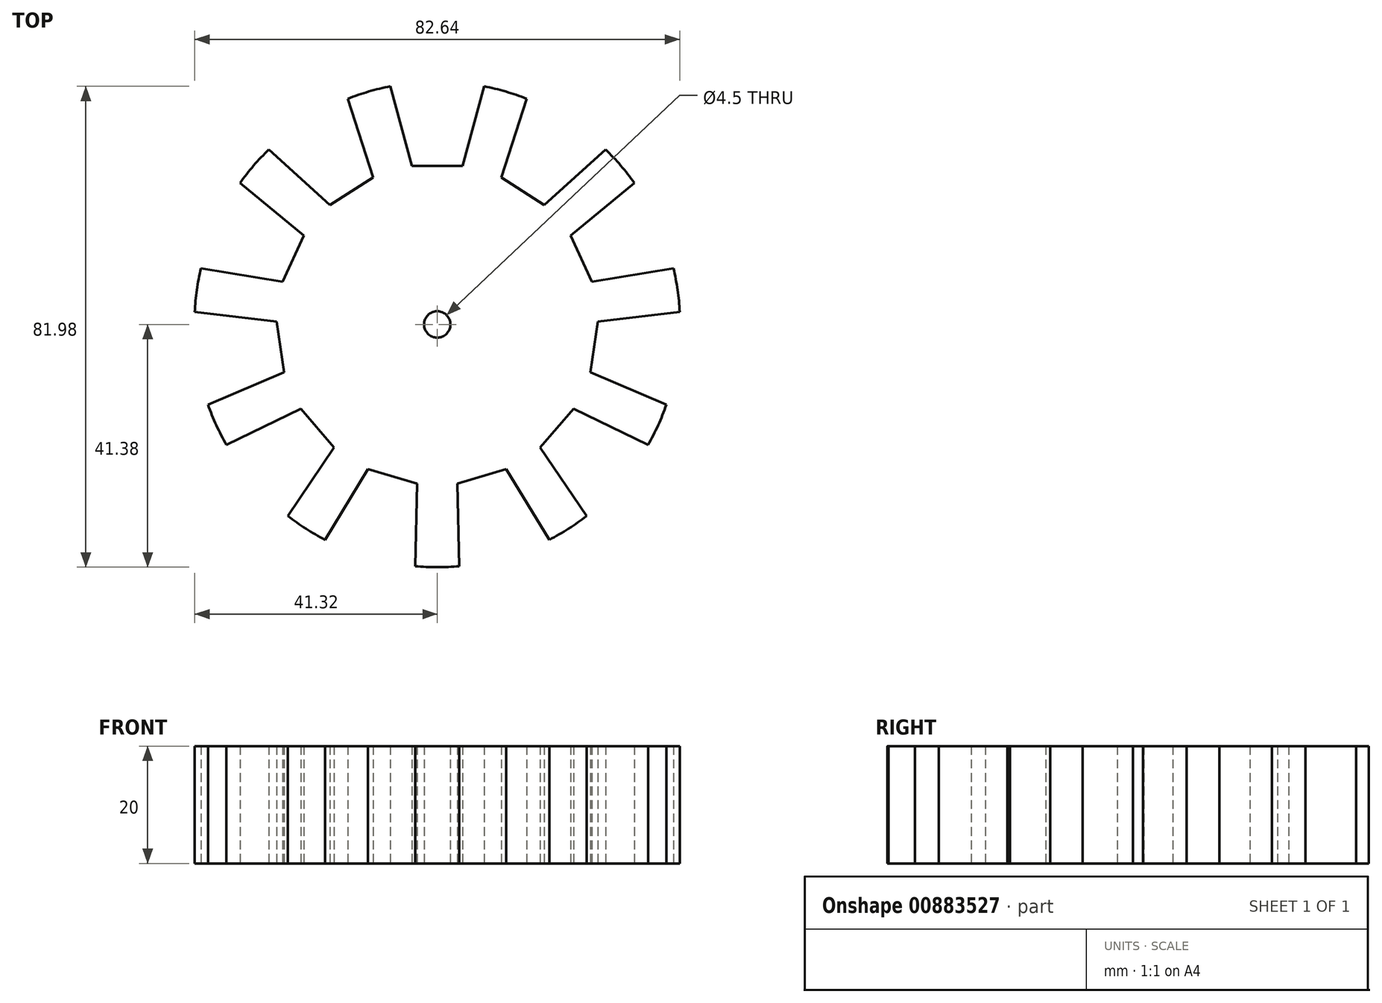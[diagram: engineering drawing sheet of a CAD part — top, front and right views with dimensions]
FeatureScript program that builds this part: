
annotation { "Feature Type Name" : "Feature", "Feature Type Description" : "" }
export const myFeature = defineFeature(function(context is Context, id is Id, definition is map)
    precondition{}
    {
        {
            var Q0;
            Q0=qCreatedBy(makeId("Top.planeOp"),FACE);
            var sketch = newSketch(context, id + "F0", { "sketchPlane" : qUnion([Q0])});
            skCircle(sketch, "E0", {"center": v(0, 0) * mm, "radius": 41.38 * mm});
            skLineSegment(sketch, "E1", {"start": v(-8, 40.6) * mm, "end": v(-4.35, 27) * mm});
            skLineSegment(sketch, "E2", {"start": v(-4.35, 27) * mm, "end": v(0, 27) * mm});
            skLineSegment(sketch, "E3.MirrorCS", {"start": v(8, 40.6) * mm, "end": v(4.35, 27) * mm});
            skLineSegment(sketch, "E4.MirrorCS", {"start": v(4.35, 27) * mm, "end": v(0, 27) * mm});
            skCircle(sketch, "E5", {"center": v(0, 0) * mm, "radius": 2.25 * mm});
            skSolve(sketch);
        }
        {
            var Q0;
            {var subQ1=sQuery(id+"F0.wireOp",EDGE,"E1");Q0=makeQuery(id+"F0.imprint","IMPRINT",FACE,{"disambiguationData":[TD([[makeQuery(id+"F0.imprint","IMPRINT",EDGE,{"derivedFrom":subQ1}),-1.0]])]});}
            extrude(context, id + "F1", {"entities" : qUnion([Q0]), "depth" : 20 * mm, "offsetDistance" : 25 * mm});
        }
        {
            var Q0;
            Q0=makeQuery(id+"F1.opExtrude","SWEPT_FACE",FACE,{"disambiguationData":[OSD([sQuery(id+"F0.wireOp",EDGE,"E1")])]});
            var Q1;
            Q1=makeQuery(id+"F1.opExtrude","SWEPT_FACE",FACE,{"disambiguationData":[OSD([sQuery(id+"F0.wireOp",EDGE,"E2"),sQuery(id+"F0.wireOp",EDGE,"E4.MirrorCS")])]});
            var Q2;
            Q2=makeQuery(id+"F1.opExtrude","SWEPT_FACE",FACE,{"disambiguationData":[OSD([sQuery(id+"F0.wireOp",EDGE,"E3.MirrorCS")])]});
            var Q3;
            Q3=makeQuery(id+"F1.opExtrude","SWEPT_FACE",FACE,{"disambiguationData":[OSD([sQuery(id+"F0.wireOp",EDGE,"E0")])]});
            circularPattern(context, id + "F2", {"patternType" : PatternType.FACE, "faces" : qUnion([Q0, Q1, Q2]), "axis" : qUnion([Q3]), "angle" : 360 * degree, "instanceCount" : 11, "equalSpace" : true});
        }
    });
